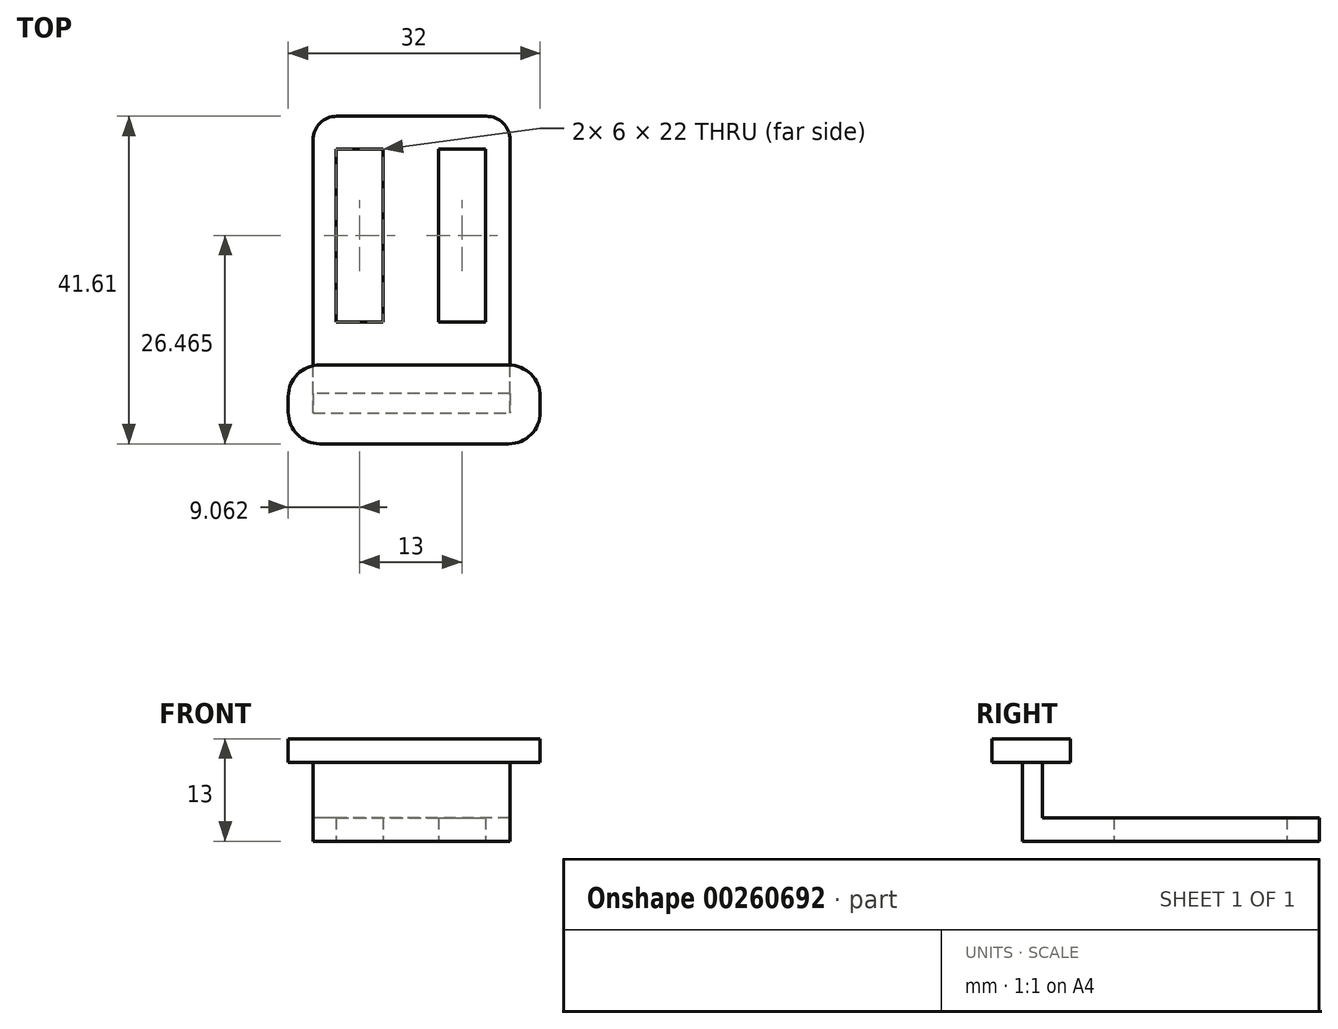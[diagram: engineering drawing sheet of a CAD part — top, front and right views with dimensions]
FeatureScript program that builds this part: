
annotation { "Feature Type Name" : "Feature", "Feature Type Description" : "" }
export const myFeature = defineFeature(function(context is Context, id is Id, definition is map)
    precondition{}
    {
        {
            var Q0;
            Q0=qCreatedBy(makeId("Top.planeOp"),FACE);
            var sketch = newSketch(context, id + "F0", { "sketchPlane" : qUnion([Q0])});
            skLineSegment(sketch, "E0.bottom", {"start": v(-12.31, 1.17) * mm, "end": v(12.69, 1.17) * mm});
            skLineSegment(sketch, "E0.top", {"start": v(-12.31, -1.33) * mm, "end": v(12.69, -1.33) * mm});
            skLineSegment(sketch, "E0.left", {"start": v(-12.31, 1.17) * mm, "end": v(-12.31, -1.33) * mm});
            skLineSegment(sketch, "E0.right", {"start": v(12.69, 1.17) * mm, "end": v(12.69, -1.33) * mm});
            skLineSegment(sketch, "E1.bottom", {"start": v(-15.47, 4.77) * mm, "end": v(16.53, 4.77) * mm});
            skLineSegment(sketch, "E1.top", {"start": v(-15.47, -5.23) * mm, "end": v(16.53, -5.23) * mm});
            skLineSegment(sketch, "E1.left", {"start": v(-15.47, 4.77) * mm, "end": v(-15.47, -5.23) * mm});
            skLineSegment(sketch, "E1.right", {"start": v(16.53, 4.77) * mm, "end": v(16.53, -5.23) * mm});
            skLineSegment(sketch, "E2", {"start": v(-12.31, 1.17) * mm, "end": v(-12.31, 36.38) * mm});
            skLineSegment(sketch, "E3", {"start": v(12.69, 1.17) * mm, "end": v(12.69, 36.38) * mm});
            skLineSegment(sketch, "E4", {"start": v(-12.31, 36.38) * mm, "end": v(12.69, 36.38) * mm});
            skLineSegment(sketch, "E5.bottom", {"start": v(-9.4, 32.24) * mm, "end": v(-3.4, 32.24) * mm});
            skLineSegment(sketch, "E5.top", {"start": v(-9.4, 10.24) * mm, "end": v(-3.4, 10.24) * mm});
            skLineSegment(sketch, "E5.left", {"start": v(-9.4, 32.24) * mm, "end": v(-9.4, 10.24) * mm});
            skLineSegment(sketch, "E5.right", {"start": v(-3.4, 32.24) * mm, "end": v(-3.4, 10.24) * mm});
            skLineSegment(sketch, "E6.bottom", {"start": v(3.6, 32.24) * mm, "end": v(9.6, 32.24) * mm});
            skLineSegment(sketch, "E6.top", {"start": v(3.6, 10.24) * mm, "end": v(9.6, 10.24) * mm});
            skLineSegment(sketch, "E6.left", {"start": v(3.6, 32.24) * mm, "end": v(3.6, 10.24) * mm});
            skLineSegment(sketch, "E6.right", {"start": v(9.6, 32.24) * mm, "end": v(9.6, 10.24) * mm});
            skSolve(sketch);
        }
        {
            var Q0;
            {var subQ0=sQuery(id+"F0.wireOp",EDGE,"a9d801fe-b2c9-4004-b280-62f218a957da");Q0=makeQuery(id+"F0.imprint","IMPRINT",FACE,{"disambiguationData":[TD([[makeQuery(id+"F0.imprint","IMPRINT",EDGE,{"derivedFrom":subQ0}),-1.0]])]});}
            var Q1;
            {var subQ0=sQuery(id+"F0.wireOp",EDGE,"E0.bottom");Q1=makeQuery(id+"F0.imprint","IMPRINT",FACE,{"disambiguationData":[TD([[makeQuery(id+"F0.imprint","IMPRINT",EDGE,{"derivedFrom":subQ0}),1.0]])]});}
            var Q2;
            Q2=makeQuery(id+"F0.imprint","IMPRINT",FACE,{"disambiguationData":[TD([[makeQuery(id+"F0.imprint","IMPRINT",EDGE,{"derivedFrom":sQuery(id+"F0.wireOp",EDGE,"E0.bottom")}),-1.0]])]});
            var Q3;
            {var subQ0=sQuery(id+"F0.wireOp",EDGE,"E4");Q3=makeQuery(id+"F0.imprint","IMPRINT",FACE,{"disambiguationData":[TD([[makeQuery(id+"F0.imprint","IMPRINT",EDGE,{"derivedFrom":subQ0}),-1.0]])]});}
            extrude(context, id + "F1", {"entities" : qUnion([Q0, Q1, Q2, Q3]), "depth" : 3 * mm});
        }
        {
            var Q0;
            Q0=makeQuery(id+"F0.imprint","IMPRINT",FACE,{"disambiguationData":[TD([[makeQuery(id+"F0.imprint","IMPRINT",EDGE,{"derivedFrom":sQuery(id+"F0.wireOp",EDGE,"E0.bottom")}),-1.0]])]});
            extrude(context, id + "F2", {"entities" : qUnion([Q0]), "operationType" : NewBodyOperationType.ADD, "depth" : 10 * mm});
        }
        {
            var Q0;
            {var subQ0=sQuery(id+"F0.wireOp",EDGE,"E0.bottom");Q0=makeQuery(id+"F0.imprint","IMPRINT",FACE,{"disambiguationData":[TD([[makeQuery(id+"F0.imprint","IMPRINT",EDGE,{"derivedFrom":subQ0}),1.0]])]});}
            var Q1;
            Q1=makeQuery(id+"F0.imprint","IMPRINT",FACE,{"disambiguationData":[TD([[makeQuery(id+"F0.imprint","IMPRINT",EDGE,{"derivedFrom":sQuery(id+"F0.wireOp",EDGE,"E0.top")}),-1.0]])]});
            var Q2;
            Q2=makeQuery(id+"F0.imprint","IMPRINT",FACE,{"disambiguationData":[TD([[makeQuery(id+"F0.imprint","IMPRINT",EDGE,{"derivedFrom":sQuery(id+"F0.wireOp",EDGE,"E0.bottom")}),-1.0]])]});
            extrude(context, id + "F3", {"entities" : qUnion([Q0, Q1, Q2]), "operationType" : NewBodyOperationType.ADD, "depth" : 13 * mm, "hasSecondDirection" : true, "secondDirectionOppositeDirection" : false, "secondDirectionDepth" : 10 * mm});
        }
        {
            var Q0;
            Q0=makeQuery(id+"F3.opExtrude","SWEPT_EDGE",EDGE,{"disambiguationData":[OSD([sQuery(id+"F0.wireOp",EDGE,"E1.top"),sQuery(id+"F0.wireOp",EDGE,"E1.right")])]});
            var Q1;
            Q1=makeQuery(id+"F3.opExtrude","SWEPT_EDGE",EDGE,{"disambiguationData":[OSD([sQuery(id+"F0.wireOp",EDGE,"E1.bottom"),sQuery(id+"F0.wireOp",EDGE,"E1.right")])]});
            var Q2;
            Q2=makeQuery(id+"F3.opExtrude","SWEPT_EDGE",EDGE,{"disambiguationData":[OSD([sQuery(id+"F0.wireOp",EDGE,"E1.top"),sQuery(id+"F0.wireOp",EDGE,"E1.left")])]});
            var Q3;
            Q3=makeQuery(id+"F3.opExtrude","SWEPT_EDGE",EDGE,{"disambiguationData":[OSD([sQuery(id+"F0.wireOp",EDGE,"E1.bottom"),sQuery(id+"F0.wireOp",EDGE,"E1.left")])]});
            fillet(context, id + "F4", {"entities" : qUnion([Q0, Q1, Q2, Q3]), "radius" : 4 * mm, "tangentPropagation" : true, "allowEdgeOverflow" : false});
        }
        {
            var Q0;
            Q0=makeQuery(id+"F1.opExtrude","SWEPT_EDGE",EDGE,{"disambiguationData":[OSD([sQuery(id+"F0.wireOp",EDGE,"E2"),sQuery(id+"F0.wireOp",EDGE,"E4")])]});
            var Q1;
            Q1=makeQuery(id+"F1.opExtrude","SWEPT_EDGE",EDGE,{"disambiguationData":[OSD([sQuery(id+"F0.wireOp",EDGE,"E3"),sQuery(id+"F0.wireOp",EDGE,"E4")])]});
            fillet(context, id + "F5", {"entities" : qUnion([Q0, Q1]), "radius" : 3 * mm, "tangentPropagation" : true, "allowEdgeOverflow" : false});
        }
    });
